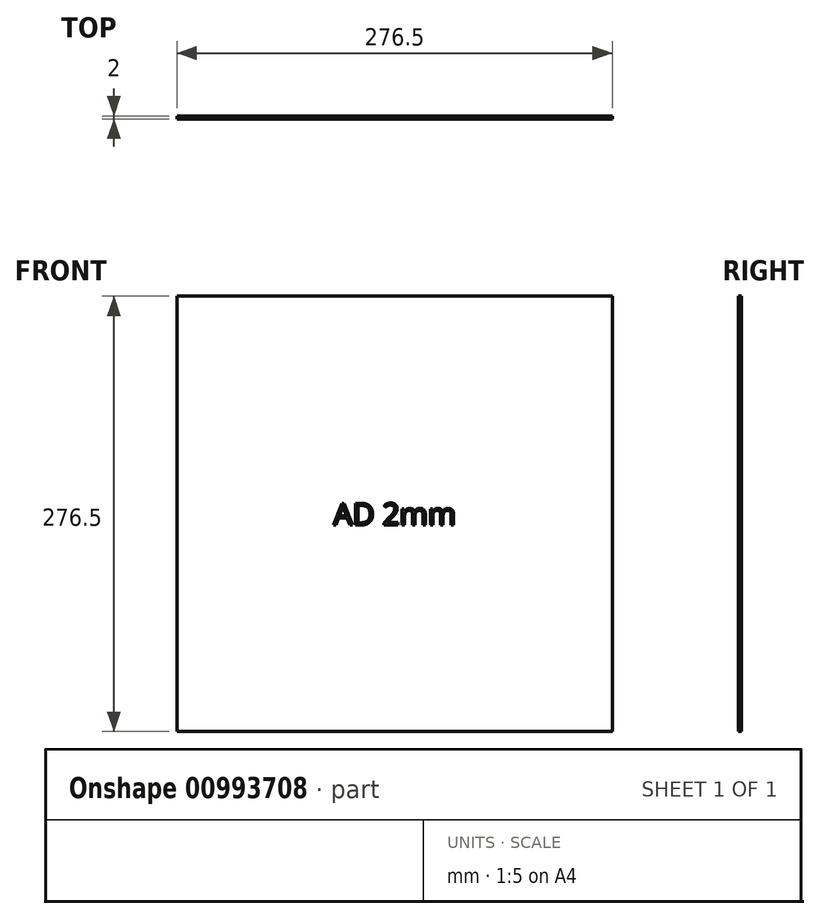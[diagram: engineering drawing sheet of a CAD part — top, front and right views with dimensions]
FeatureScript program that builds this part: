
annotation { "Feature Type Name" : "Feature", "Feature Type Description" : "" }
export const myFeature = defineFeature(function(context is Context, id is Id, definition is map)
    precondition{}
    {
        {
            var Q0;
            Q0=qCreatedBy(makeId("Front.planeOp"),FACE);
            var sketch = newSketch(context, id + "F0", { "sketchPlane" : qUnion([Q0])});
            skLineSegment(sketch, "E0.bottom", {"start": v(0, 0) * mm, "end": v(276.5, 0) * mm});
            skLineSegment(sketch, "E0.top", {"start": v(0, 276.5) * mm, "end": v(276.5, 276.5) * mm});
            skLineSegment(sketch, "E0.left", {"start": v(0, 0) * mm, "end": v(0, 276.5) * mm});
            skLineSegment(sketch, "E0.right", {"start": v(276.5, 0) * mm, "end": v(276.5, 276.5) * mm});
            skSolve(sketch);
        }
        {
            var Q0;
            Q0 = qSketchRegion(id + "F0", true);
            extrude(context, id + "F1", {"entities" : qUnion([Q0]), "depth" : 2 * mm, "offsetDistance" : 25.4 * mm});
        }
        {
            var Q0;
            Q0=makeQuery(id+"F1.opExtrude","CAP_FACE",FACE,{"disambiguationData":[OSD([sQuery(id+"F0.wireOp",EDGE,"E0.bottom"),sQuery(id+"F0.wireOp",EDGE,"E0.top"),sQuery(id+"F0.wireOp",EDGE,"E0.left"),sQuery(id+"F0.wireOp",EDGE,"E0.right")])],"isStart":false});
            var sketch = newSketch(context, id + "F2", { "sketchPlane" : qUnion([Q0])});
            skText(sketch, "E1", { "text": "AD 2mm", "fontName": "OpenSans-Regular.ttf"});
            skPoint(sketch, "E2", {"position": v(138.25, 138.25) * mm});
            skPoint(sketch, "E2.positionSnap0", {"position": v(0, 138.25) * mm});
            skPoint(sketch, "E2.positionSnap1", {"position": v(138.25, 276.5) * mm});
            const initialGuessF2  = {"E1": [0.09932, 0.13123, 1, 0, 0.01384]};
            skSetInitialGuess(sketch, initialGuessF2);
            skSolve(sketch);
        }
        {
            var Q0;
            Q0 = qSketchRegion(id + "F2", true);
            extrude(context, id + "F3", {"entities" : qUnion([Q0]), "operationType" : NewBodyOperationType.REMOVE, "oppositeDirection" : true, "depth" : 1 * mm, "offsetDistance" : 25.4 * mm});
        }
    });
